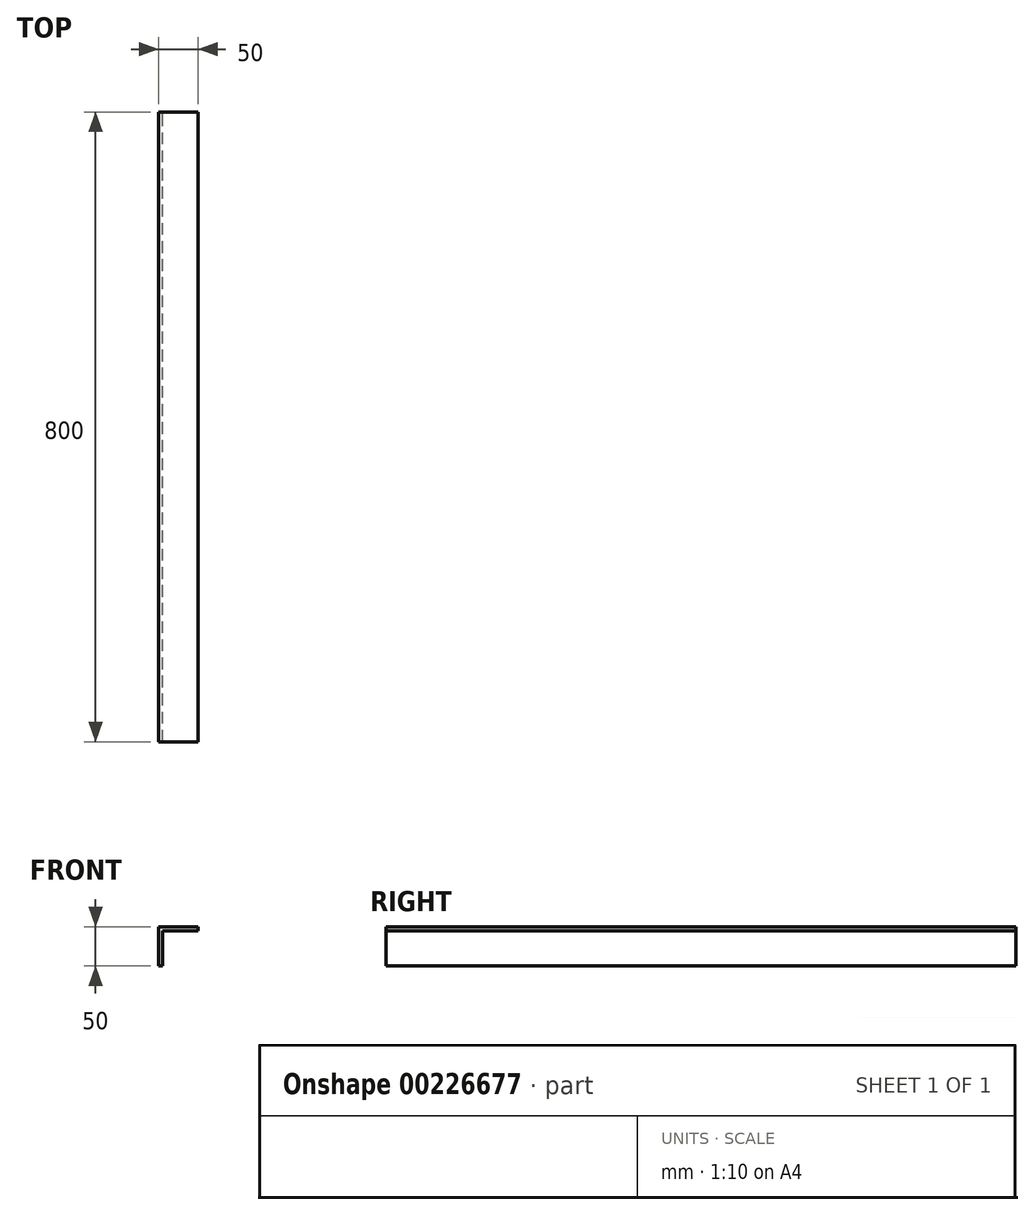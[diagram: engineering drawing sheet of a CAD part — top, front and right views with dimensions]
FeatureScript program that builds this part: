
annotation { "Feature Type Name" : "Feature", "Feature Type Description" : "" }
export const myFeature = defineFeature(function(context is Context, id is Id, definition is map)
    precondition{}
    {
        {
            var Q0;
            Q0=qCreatedBy(makeId("Front.planeOp"),FACE);
            var sketch = newSketch(context, id + "F0", { "sketchPlane" : qUnion([Q0])});
            skLineSegment(sketch, "E0", {"start": v(-25.74, -48.67) * mm, "end": v(-25.74, 1.33) * mm});
            skLineSegment(sketch, "E1", {"start": v(-25.74, 1.33) * mm, "end": v(24.26, 1.33) * mm});
            skLineSegment(sketch, "E2", {"start": v(-25.74, -48.67) * mm, "end": v(-20.74, -48.67) * mm});
            skLineSegment(sketch, "E3", {"start": v(24.26, 1.33) * mm, "end": v(24.26, -3.67) * mm});
            skLineSegment(sketch, "E4", {"start": v(24.26, -3.67) * mm, "end": v(-20.74, -3.67) * mm});
            skLineSegment(sketch, "E5", {"start": v(-20.74, -3.67) * mm, "end": v(-20.74, -48.67) * mm});
            skSolve(sketch);
        }
        {
            var Q0;
            Q0=makeQuery(id+"F0.imprint","IMPRINT",FACE,{"disambiguationData":[TD([[makeQuery(id+"F0.imprint","IMPRINT",EDGE,{"derivedFrom":sQuery(id+"F0.wireOp",EDGE,"E0")}),-1.0]])]});
            extrude(context, id + "F1", {"entities" : qUnion([Q0]), "depth" : 800 * mm});
        }
    });
